FCSTD DOCUMENT  (FreeCAD 0.19R24291 (Git))
Label: spoon
License: All rights reserved
LicenseURL: http://en.wikipedia.org/wiki/All_rights_reserved
objects: Sketcher::SketchObject×2, PartDesign::Body×1
note: 3 computed .brp shape members not serialized (recipe doc carries the construction recipe); baked Part::Feature solids carry a one-line shape summary decoded from their .brp

FEATURE [Sketcher::SketchObject] Sketch  label="Top Profile"
  FullyConstrained = true
  MapMode = 5
  Support = -> [XY_Plane]
  sketch-geometry (12):
    g0: ArcOfCircle CenterX=-9e-16 CenterY=10 CenterZ=0 NormalX=0 NormalY=0 NormalZ=1 AngleXU=0 Radius=10 StartAngle=3.14159 EndAngle=4.71239
    g1: LineSegment StartX=-10 StartY=10 StartZ=0 EndX=-10 EndY=180 EndZ=0
    g2: ArcOfCircle CenterX=-40 CenterY=180 CenterZ=0 NormalX=0 NormalY=0 NormalZ=1 AngleXU=0 Radius=30 StartAngle=4e-16 EndAngle=0.87504
    g3: ArcOfCircle CenterX=11.2773 CenterY=241.406 CenterZ=0 NormalX=0 NormalY=0 NormalZ=1 AngleXU=0 Radius=50 StartAngle=3.44089 EndAngle=4.01663
    g4: ArcOfCircle CenterX=-11.2773 CenterY=241.406 CenterZ=0 NormalX=0 NormalY=0 NormalZ=1 AngleXU=0 Radius=50 StartAngle=5.40814 EndAngle=5.98389
    g5: ArcOfCircle CenterX=-9e-16 CenterY=10 CenterZ=0 NormalX=0 NormalY=0 NormalZ=1 AngleXU=0 Radius=10 StartAngle=4.71239 EndAngle=6.28319
    g6: LineSegment StartX=10 StartY=10 StartZ=0 EndX=10 EndY=180 EndZ=0
    g7: ArcOfCircle CenterX=40 CenterY=180 CenterZ=0 NormalX=0 NormalY=0 NormalZ=1 AngleXU=0 Radius=30 StartAngle=2.26655 EndAngle=3.14159
    g8: ArcOfCircle CenterX=30.3882 CenterY=247.302 CenterZ=0 NormalX=0 NormalY=0 NormalZ=1 AngleXU=0 Radius=70 StartAngle=2.606 EndAngle=3.44089
    g9: ArcOfCircle CenterX=7.2e-15 CenterY=265.336 CenterZ=0 NormalX=0 NormalY=0 NormalZ=1 AngleXU=0 Radius=34.6635 StartAngle=1.5708 EndAngle=2.606
    g10: ArcOfCircle CenterX=-30.3882 CenterY=247.302 CenterZ=0 NormalX=0 NormalY=0 NormalZ=1 AngleXU=0 Radius=70 StartAngle=5.98389 EndAngle=6.81878
    g11: ArcOfCircle CenterX=7.2e-15 CenterY=265.336 CenterZ=0 NormalX=0 NormalY=0 NormalZ=1 AngleXU=0 Radius=34.6635 StartAngle=0.535594 EndAngle=1.5708
  constraints (29):
    c: PointOnObject(g0,g-2)
    c: Vertical(g1)
    c: Tangent(g3,g2) = 1.5708
    c: Tangent(g2,g1) = -1.5708
    c: Tangent(g1,g0) = 1.5708
    c: Tangent(g4,g7) = 1.5708
    c: Tangent(g7,g6) = 1.5708
    c: Tangent(g6,g5) = -1.5708
    c: Symmetric(g2,g4,g-2)
    c: Symmetric(g1,g6,g-2)
    c: Tangent(g5,g0) = -1.5708
    c: Symmetric(g0,g5,g-2)
    c: Symmetric(g4,g3,g-2)
    c: PointOnObject(g9,g-2)
    c: Tangent(g8,g3) = -1.5708
    c: Tangent(g9,g8) = -1.5708
    c: Tangent(g11,g10) = -1.5708
    c: Symmetric(g8,g10,g-2)
    c: DistanceY(g-1,g0) = 0
    c: Radius(g0) = 10
    c: Radius(g3) = 50
    c: Tangent(g9,g11) = -1.5708
    c: Radius(g2) = 30
    c: Tangent(g10,g4) = -1.5708
    c: DistanceY(g9) = 300
    c: DistanceY(g6,g9) = 120
    c: DistanceX(g3,g4) = 73
    c: DistanceY(g4,g10) = 80
    c: Radius(g8) = 70
FEATURE [Sketcher::SketchObject] Sketch001  label="Side Profile"
  ExternalGeometry = -> [Sketch]
  FullyConstrained = true
  MapMode = 5
  Placement = pos=(0,0,0) rot=(0.57735,0.57735,0.57735;2.0944rad)
  Support = -> [YZ_Plane]
  sketch-geometry (8):
    g0: ArcOfCircle CenterX=240.835 CenterY=41.8873 CenterZ=0 NormalX=0 NormalY=0 NormalZ=1 AngleXU=0 Radius=77 StartAngle=4.7665 EndAngle=5.59824
    g1: ArcOfCircle CenterX=241.484 CenterY=29.9049 CenterZ=0 NormalX=0 NormalY=0 NormalZ=1 AngleXU=0 Radius=65 StartAngle=3.96813 EndAngle=4.7665
    g2: ArcOfCircle CenterX=190 CenterY=-26 CenterZ=0 NormalX=0 NormalY=0 NormalZ=1 AngleXU=0 Radius=11 StartAngle=0.826538 EndAngle=1.5708
    g3: LineSegment StartX=190 StartY=-15 StartZ=0 EndX=55 EndY=-15 EndZ=0
    g4: ArcOfCircle CenterX=296.596 CenterY=-3.66228 CenterZ=0 NormalX=0 NormalY=0 NormalZ=1 AngleXU=0 Radius=5 StartAngle=5.59824 EndAngle=7.10511
    g5: ArcOfCircle CenterX=12.444 CenterY=-1.18164 CenterZ=0 NormalX=0 NormalY=0 NormalZ=1 AngleXU=0 Radius=12.5 StartAngle=3.04692 EndAngle=4.65045
    g6: ArcOfCircle CenterX=55 CenterY=685 CenterZ=0 NormalX=0 NormalY=0 NormalZ=1 AngleXU=0 Radius=700 StartAngle=4.65045 EndAngle=4.71239
    g7: LineSegment StartX=0 StartY=-2.2e-15 StartZ=0 EndX=300 EndY=8.39e-14 EndZ=0
  constraints (22):
    c: Horizontal(g3)
    c: Tangent(g3,g2) = -1.5708
    c: Tangent(g2,g1) = 1.5708
    c: Tangent(g1,g0) = -1.5708
    c: Coincident(g4,g-3)
    c: Tangent(g0,g4) = -1.5708
    c: Radius(g1) = 65
    c: Radius(g0) = 77
    c: Tangent(g6,g5) = -1.5708
    c: Tangent(g6,g3) = 1.5708
    c: DistanceY(g3,g-1) = 15
    c: Coincident(g-1,g5)
    c: Coincident(g7,g4)
    c: Radius(g5) = 12.5
    c: Radius(g6) = 700
    c: Radius(g2) = 11
    c: Radius(g4) = 5
    c: DistanceX(g-1,g3) = 55
    c: DistanceY(g0,g-1) = 35
    c: DistanceX(g-1,g2) = 190
    c: DistanceX(g2,g0) = 55
    c: Coincident(g5,g7)
FEATURE [PartDesign::Body] Body
  Group = -> [Sketch,Sketch001]
  Origin = -> Origin
